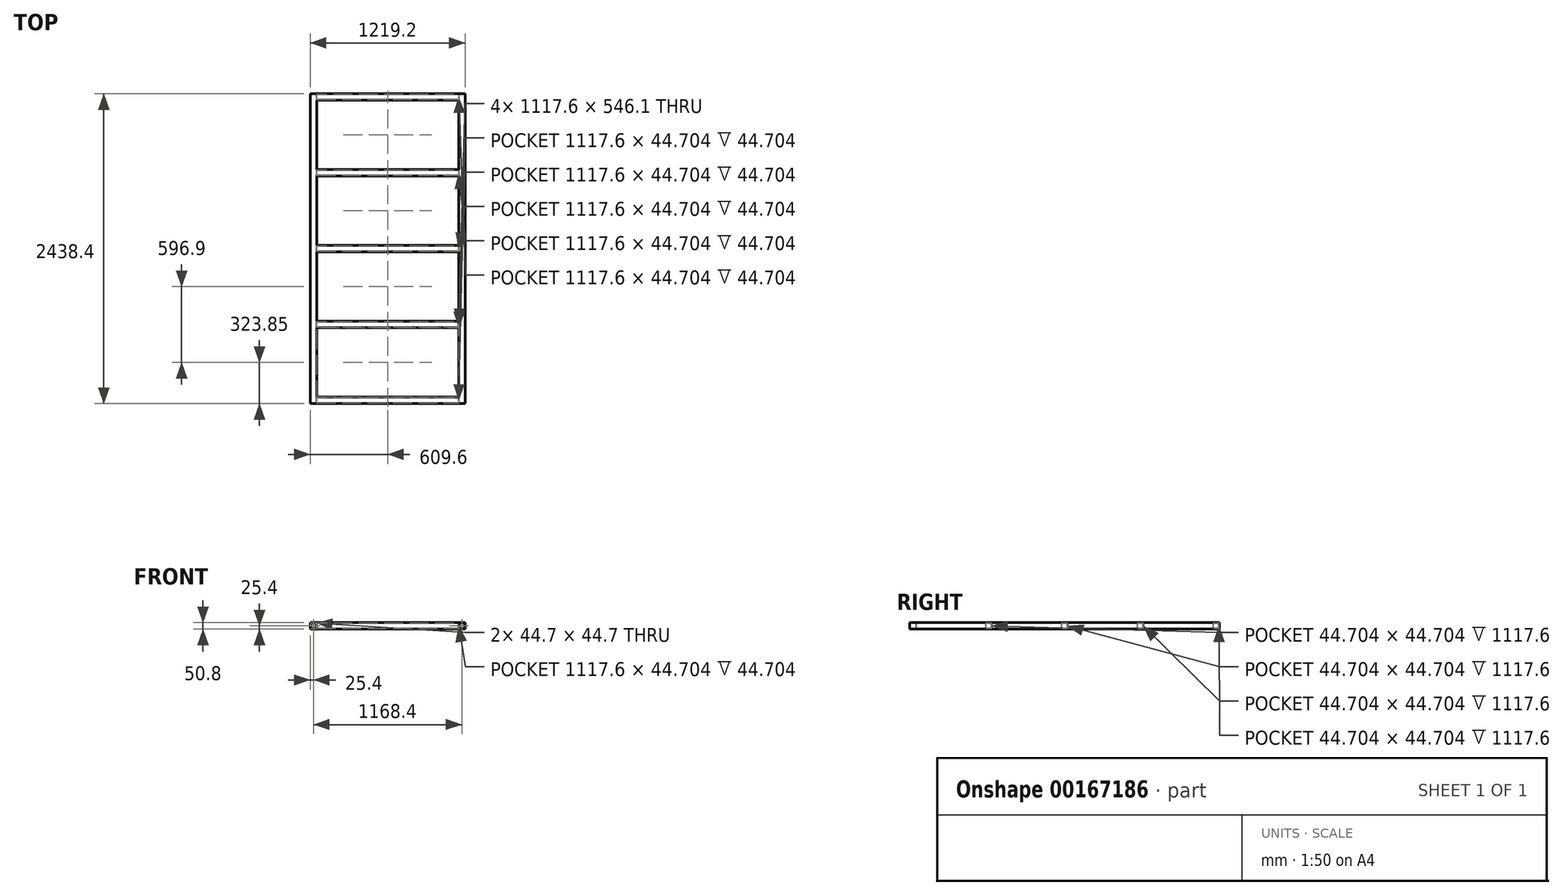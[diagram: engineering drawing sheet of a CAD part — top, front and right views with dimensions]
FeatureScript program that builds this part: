
annotation { "Feature Type Name" : "Feature", "Feature Type Description" : "" }
export const myFeature = defineFeature(function(context is Context, id is Id, definition is map)
    precondition{}
    {
        {
            var Q0;
            Q0=qCreatedBy(makeId("Front.planeOp"),FACE);
            var sketch = newSketch(context, id + "F0", { "sketchPlane" : qUnion([Q0])});
            skLineSegment(sketch, "E0.bottom", {"start": v(-609.6, 0) * mm, "end": v(-558.8, 0) * mm});
            skLineSegment(sketch, "E0.top", {"start": v(-609.6, 50.8) * mm, "end": v(-558.8, 50.8) * mm});
            skLineSegment(sketch, "E0.left", {"start": v(-609.6, 0) * mm, "end": v(-609.6, 50.8) * mm});
            skLineSegment(sketch, "E0.right", {"start": v(-558.8, 0) * mm, "end": v(-558.8, 50.8) * mm});
            skLineSegment(sketch, "E1.bottom", {"start": v(-606.55, 3.05) * mm, "end": v(-561.85, 3.05) * mm});
            skLineSegment(sketch, "E1.top", {"start": v(-606.55, 47.75) * mm, "end": v(-561.85, 47.75) * mm});
            skLineSegment(sketch, "E1.left", {"start": v(-606.55, 3.05) * mm, "end": v(-606.55, 47.75) * mm});
            skLineSegment(sketch, "E1.right", {"start": v(-561.85, 3.05) * mm, "end": v(-561.85, 47.75) * mm});
            skLineSegment(sketch, "E2.MirrorCS", {"start": v(609.6, 0) * mm, "end": v(558.8, 0) * mm});
            skLineSegment(sketch, "E3.MirrorCS", {"start": v(609.6, 0) * mm, "end": v(609.6, 50.8) * mm});
            skLineSegment(sketch, "E4.MirrorCS", {"start": v(561.85, 3.05) * mm, "end": v(561.85, 47.75) * mm});
            skLineSegment(sketch, "E5.MirrorCS", {"start": v(606.55, 3.05) * mm, "end": v(606.55, 47.75) * mm});
            skLineSegment(sketch, "E6.MirrorCS", {"start": v(609.6, 50.8) * mm, "end": v(558.8, 50.8) * mm});
            skLineSegment(sketch, "E7.MirrorCS", {"start": v(558.8, 0) * mm, "end": v(558.8, 50.8) * mm});
            skLineSegment(sketch, "E8.MirrorCS", {"start": v(606.55, 47.75) * mm, "end": v(561.85, 47.75) * mm});
            skLineSegment(sketch, "E9.MirrorCS", {"start": v(606.55, 3.05) * mm, "end": v(561.85, 3.05) * mm});
            skSolve(sketch);
        }
        {
            var Q0;
            Q0=makeQuery(id+"F0.imprint","IMPRINT",FACE,{"disambiguationData":[TD([[makeQuery(id+"F0.imprint","IMPRINT",EDGE,{"derivedFrom":sQuery(id+"F0.wireOp",EDGE,"E1.bottom")}),1.0]])]});
            var Q1;
            Q1=makeQuery(id+"F0.imprint","IMPRINT",FACE,{"disambiguationData":[TD([[makeQuery(id+"F0.imprint","IMPRINT",EDGE,{"derivedFrom":sQuery(id+"F0.wireOp",EDGE,"E0.bottom")}),1.0]])]});
            var Q2;
            Q2=makeQuery(id+"F0.imprint","IMPRINT",FACE,{"disambiguationData":[TD([[makeQuery(id+"F0.imprint","IMPRINT",EDGE,{"derivedFrom":sQuery(id+"F0.wireOp",EDGE,"E4.MirrorCS")}),-1.0]])]});
            var Q3;
            Q3=makeQuery(id+"F0.imprint","IMPRINT",FACE,{"disambiguationData":[TD([[makeQuery(id+"F0.imprint","IMPRINT",EDGE,{"derivedFrom":sQuery(id+"F0.wireOp",EDGE,"E2.MirrorCS")}),-1.0]])]});
            extrude(context, id + "F1", {"entities" : qUnion([Q0, Q1, Q2, Q3]), "depth" : 2438.4 * mm});
        }
        {
            var Q0;
            Q0=makeQuery(id+"F0.imprint","IMPRINT",FACE,{"disambiguationData":[TD([[makeQuery(id+"F0.imprint","IMPRINT",EDGE,{"derivedFrom":sQuery(id+"F0.wireOp",EDGE,"E1.bottom")}),1.0]])]});
            var Q1;
            Q1=makeQuery(id+"F0.imprint","IMPRINT",FACE,{"disambiguationData":[TD([[makeQuery(id+"F0.imprint","IMPRINT",EDGE,{"derivedFrom":sQuery(id+"F0.wireOp",EDGE,"E4.MirrorCS")}),-1.0]])]});
            extrude(context, id + "F2", {"entities" : qUnion([Q0, Q1]), "operationType" : NewBodyOperationType.REMOVE, "depth" : 2438.4 * mm});
        }
        {
            var Q0;
            Q0=makeQuery(id+"F1.opExtrude","SWEPT_FACE",FACE,{"disambiguationData":[OSD([sQuery(id+"F0.wireOp",EDGE,"E0.right")])]});
            var sketch = newSketch(context, id + "F3", { "sketchPlane" : qUnion([Q0])});
            skLineSegment(sketch, "E10.bottom", {"start": v(-2438.4, 50.8) * mm, "end": v(-2387.6, 50.8) * mm});
            skLineSegment(sketch, "E10.top", {"start": v(-2438.4, 0) * mm, "end": v(-2387.6, 0) * mm});
            skLineSegment(sketch, "E10.left", {"start": v(-2438.4, 50.8) * mm, "end": v(-2438.4, 0) * mm});
            skLineSegment(sketch, "E10.right", {"start": v(-2387.6, 50.8) * mm, "end": v(-2387.6, 0) * mm});
            skLineSegment(sketch, "E11.bottom", {"start": v(-2435.35, 47.75) * mm, "end": v(-2390.65, 47.75) * mm});
            skLineSegment(sketch, "E11.top", {"start": v(-2435.35, 3.05) * mm, "end": v(-2390.65, 3.05) * mm});
            skLineSegment(sketch, "E11.left", {"start": v(-2435.35, 47.75) * mm, "end": v(-2435.35, 3.05) * mm});
            skLineSegment(sketch, "E11.right", {"start": v(-2390.65, 47.75) * mm, "end": v(-2390.65, 3.05) * mm});
            skLineSegment(sketch, "E12.1.0.0", {"start": v(-1838.45, 3.05) * mm, "end": v(-1793.75, 3.05) * mm});
            skLineSegment(sketch, "E12.1.0.1", {"start": v(-1841.5, 0) * mm, "end": v(-1790.7, 0) * mm});
            skLineSegment(sketch, "E12.1.0.2", {"start": v(-1841.5, 50.8) * mm, "end": v(-1790.7, 50.8) * mm});
            skLineSegment(sketch, "E12.1.0.3", {"start": v(-1841.5, 50.8) * mm, "end": v(-1841.5, 0) * mm});
            skLineSegment(sketch, "E12.1.0.4", {"start": v(-1838.45, 47.75) * mm, "end": v(-1838.45, 3.05) * mm});
            skLineSegment(sketch, "E12.1.0.5", {"start": v(-1790.7, 50.8) * mm, "end": v(-1790.7, 0) * mm});
            skLineSegment(sketch, "E12.1.0.6", {"start": v(-1838.45, 47.75) * mm, "end": v(-1793.75, 47.75) * mm});
            skLineSegment(sketch, "E12.1.0.7", {"start": v(-1793.75, 47.75) * mm, "end": v(-1793.75, 3.05) * mm});
            skLineSegment(sketch, "E12.2.0.0", {"start": v(-1241.55, 3.05) * mm, "end": v(-1196.85, 3.05) * mm});
            skLineSegment(sketch, "E12.2.0.1", {"start": v(-1244.6, 0) * mm, "end": v(-1193.8, 0) * mm});
            skLineSegment(sketch, "E12.2.0.2", {"start": v(-1244.6, 50.8) * mm, "end": v(-1193.8, 50.8) * mm});
            skLineSegment(sketch, "E12.2.0.3", {"start": v(-1244.6, 50.8) * mm, "end": v(-1244.6, 0) * mm});
            skLineSegment(sketch, "E12.2.0.4", {"start": v(-1241.55, 47.75) * mm, "end": v(-1241.55, 3.05) * mm});
            skLineSegment(sketch, "E12.2.0.5", {"start": v(-1193.8, 50.8) * mm, "end": v(-1193.8, 0) * mm});
            skLineSegment(sketch, "E12.2.0.6", {"start": v(-1241.55, 47.75) * mm, "end": v(-1196.85, 47.75) * mm});
            skLineSegment(sketch, "E12.2.0.7", {"start": v(-1196.85, 47.75) * mm, "end": v(-1196.85, 3.05) * mm});
            skLineSegment(sketch, "E12.3.0.0", {"start": v(-644.65, 3.05) * mm, "end": v(-599.95, 3.05) * mm});
            skLineSegment(sketch, "E12.3.0.1", {"start": v(-647.7, 0) * mm, "end": v(-596.9, 0) * mm});
            skLineSegment(sketch, "E12.3.0.2", {"start": v(-647.7, 50.8) * mm, "end": v(-596.9, 50.8) * mm});
            skLineSegment(sketch, "E12.3.0.3", {"start": v(-647.7, 50.8) * mm, "end": v(-647.7, 0) * mm});
            skLineSegment(sketch, "E12.3.0.4", {"start": v(-644.65, 47.75) * mm, "end": v(-644.65, 3.05) * mm});
            skLineSegment(sketch, "E12.3.0.5", {"start": v(-596.9, 50.8) * mm, "end": v(-596.9, 0) * mm});
            skLineSegment(sketch, "E12.3.0.6", {"start": v(-644.65, 47.75) * mm, "end": v(-599.95, 47.75) * mm});
            skLineSegment(sketch, "E12.3.0.7", {"start": v(-599.95, 47.75) * mm, "end": v(-599.95, 3.05) * mm});
            skLineSegment(sketch, "E12.4.0.0", {"start": v(-47.75, 3.05) * mm, "end": v(-3.05, 3.05) * mm});
            skLineSegment(sketch, "E12.4.0.1", {"start": v(-50.8, 0) * mm, "end": v(0, 0) * mm});
            skLineSegment(sketch, "E12.4.0.2", {"start": v(-50.8, 50.8) * mm, "end": v(0, 50.8) * mm});
            skLineSegment(sketch, "E12.4.0.3", {"start": v(-50.8, 50.8) * mm, "end": v(-50.8, 0) * mm});
            skLineSegment(sketch, "E12.4.0.4", {"start": v(-47.75, 47.75) * mm, "end": v(-47.75, 3.05) * mm});
            skLineSegment(sketch, "E12.4.0.5", {"start": v(0, 50.8) * mm, "end": v(0, 0) * mm});
            skLineSegment(sketch, "E12.4.0.6", {"start": v(-47.75, 47.75) * mm, "end": v(-3.05, 47.75) * mm});
            skLineSegment(sketch, "E12.4.0.7", {"start": v(-3.05, 47.75) * mm, "end": v(-3.05, 3.05) * mm});
            skLineSegment(sketch, "E12.direction1", {"start": v(-2438.4, 0) * mm, "end": v(-1841.5, 0) * mm, "construction": true});
            skSolve(sketch);
        }
        {
            var Q0;
            Q0=makeQuery(id+"F3.imprint","IMPRINT",FACE,{"disambiguationData":[TD([[makeQuery(id+"F3.imprint","IMPRINT",EDGE,{"derivedFrom":sQuery(id+"F3.wireOp",EDGE,"E10.bottom")}),-1.0]])]});
            var Q1;
            Q1=makeQuery(id+"F3.imprint","IMPRINT",FACE,{"disambiguationData":[TD([[makeQuery(id+"F3.imprint","IMPRINT",EDGE,{"derivedFrom":sQuery(id+"F3.wireOp",EDGE,"E12.1.0.0")}),-1.0]])]});
            var Q2;
            Q2=makeQuery(id+"F3.imprint","IMPRINT",FACE,{"disambiguationData":[TD([[makeQuery(id+"F3.imprint","IMPRINT",EDGE,{"derivedFrom":sQuery(id+"F3.wireOp",EDGE,"E12.2.0.0")}),-1.0]])]});
            var Q3;
            Q3=makeQuery(id+"F3.imprint","IMPRINT",FACE,{"disambiguationData":[TD([[makeQuery(id+"F3.imprint","IMPRINT",EDGE,{"derivedFrom":sQuery(id+"F3.wireOp",EDGE,"E12.3.0.0")}),-1.0]])]});
            var Q4;
            Q4=makeQuery(id+"F3.imprint","IMPRINT",FACE,{"disambiguationData":[TD([[makeQuery(id+"F3.imprint","IMPRINT",EDGE,{"derivedFrom":sQuery(id+"F3.wireOp",EDGE,"E12.4.0.0")}),-1.0]])]});
            extrude(context, id + "F4", {"entities" : qUnion([Q0, Q1, Q2, Q3, Q4]), "operationType" : NewBodyOperationType.ADD, "endBound" : BoundingType.UP_TO_NEXT, "depth" : 25.4 * mm});
        }
    });
